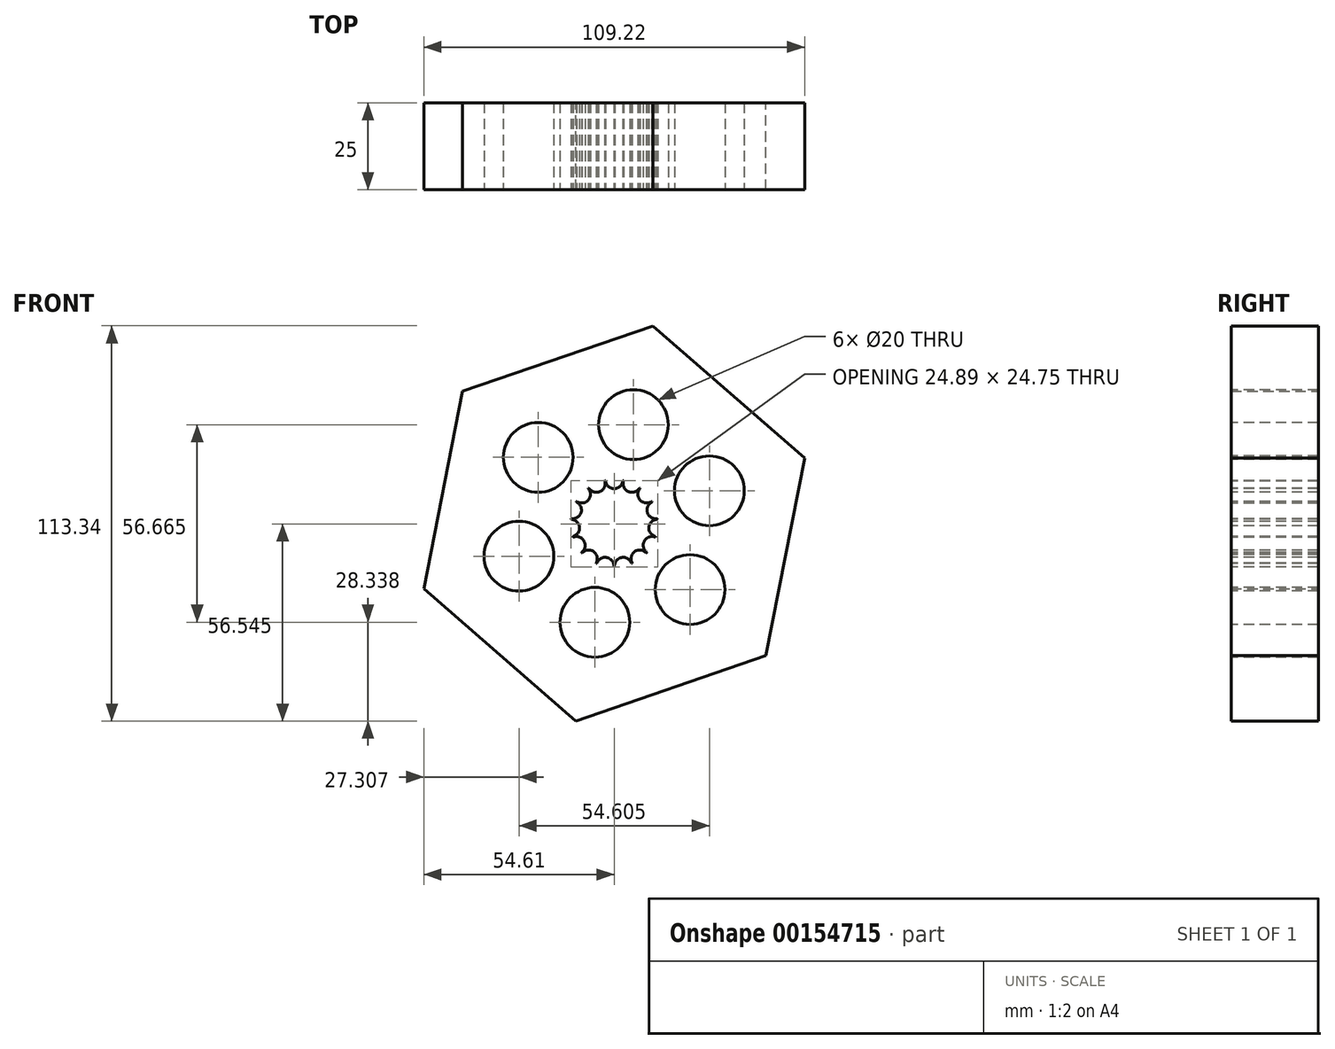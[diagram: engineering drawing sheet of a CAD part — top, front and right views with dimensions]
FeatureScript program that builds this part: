
annotation { "Feature Type Name" : "Feature", "Feature Type Description" : "" }
export const myFeature = defineFeature(function(context is Context, id is Id, definition is map)
    precondition{}
    {
        {
            var Q0;
            Q0=qCreatedBy(makeId("Front.planeOp"),FACE);
            var sketch = newSketch(context, id + "F0", { "sketchPlane" : qUnion([Q0])});
            skCircle(sketch, "E0.cCircle", {"center": v(0, 0) * mm, "radius": 50 * mm, "construction": true});
            skLineSegment(sketch, "E0.0", {"start": v(-11.06, -56.67) * mm, "end": v(-54.6, -18.75) * mm});
            skLineSegment(sketch, "E0.1", {"start": v(-54.6, -18.75) * mm, "end": v(-43.54, 37.91) * mm});
            skLineSegment(sketch, "E0.2", {"start": v(-43.54, 37.91) * mm, "end": v(11.06, 56.67) * mm});
            skLineSegment(sketch, "E0.3", {"start": v(11.06, 56.67) * mm, "end": v(54.6, 18.75) * mm});
            skLineSegment(sketch, "E0.4", {"start": v(54.6, 18.75) * mm, "end": v(43.54, -37.91) * mm});
            skLineSegment(sketch, "E0.5", {"start": v(43.54, -37.91) * mm, "end": v(-11.06, -56.67) * mm});
            skPoint(sketch, "E0.0.midPoint", {"position": v(-32.83, -37.7) * mm});
            skSolve(sketch);
        }
        {
            var Q0;
            Q0=makeQuery(id+"F0.imprint","IMPRINT",FACE,{"disambiguationData":[TD([[makeQuery(id+"F0.imprint","IMPRINT",EDGE,{"derivedFrom":sQuery(id+"F0.wireOp",EDGE,"E0.0")}),-1.0]])]});
            extrude(context, id + "F1", {"entities" : qUnion([Q0]), "endBound" : BoundingType.SYMMETRIC, "depth" : 25 * mm});
        }
        {
            var Q0;
            Q0=makeQuery(id+"F1.opExtrude","CAP_FACE",FACE,{"disambiguationData":[OSD([sQuery(id+"F0.wireOp",EDGE,"E0.0"),sQuery(id+"F0.wireOp",EDGE,"E0.1"),sQuery(id+"F0.wireOp",EDGE,"E0.2"),sQuery(id+"F0.wireOp",EDGE,"E0.3"),sQuery(id+"F0.wireOp",EDGE,"E0.4"),sQuery(id+"F0.wireOp",EDGE,"E0.5")])],"isStart":false});
            var sketch = newSketch(context, id + "F2", { "sketchPlane" : qUnion([Q0])});
            skLineSegment(sketch, "E1", {"start": v(-43.54, 37.91) * mm, "end": v(54.6, 18.75) * mm, "construction": true});
            skLineSegment(sketch, "E2", {"start": v(-11.06, -56.67) * mm, "end": v(11.06, 56.67) * mm, "construction": true});
            skLineSegment(sketch, "E3", {"start": v(-54.6, -18.75) * mm, "end": v(43.54, -37.91) * mm, "construction": true});
            skCircle(sketch, "E4", {"center": v(5.53, 28.33) * mm, "radius": 10 * mm});
            skCircle(sketch, "E5.1.0", {"center": v(-21.77, 18.96) * mm, "radius": 10 * mm});
            skCircle(sketch, "E5.2.0", {"center": v(-27.3, -9.38) * mm, "radius": 10 * mm});
            skCircle(sketch, "E5.3.0", {"center": v(-5.53, -28.33) * mm, "radius": 10 * mm});
            skCircle(sketch, "E5.4.0", {"center": v(21.77, -18.96) * mm, "radius": 10 * mm});
            skCircle(sketch, "E5.5.0", {"center": v(27.3, 9.38) * mm, "radius": 10 * mm});
            skPoint(sketch, "E5.center", {"position": v(0, 0) * mm});
            skSolve(sketch);
        }
        {
            var Q0;
            Q0=makeQuery(id+"F2.imprint","IMPRINT",FACE,{"disambiguationData":[TD([[makeQuery(id+"F2.imprint","IMPRINT",EDGE,{"derivedFrom":sQuery(id+"F2.wireOp",EDGE,"E4")}),1.0]])]});
            var Q1;
            Q1=makeQuery(id+"F2.imprint","IMPRINT",FACE,{"disambiguationData":[TD([[makeQuery(id+"F2.imprint","IMPRINT",EDGE,{"derivedFrom":sQuery(id+"F2.wireOp",EDGE,"E5.5.0")}),1.0]])]});
            var Q2;
            Q2=makeQuery(id+"F2.imprint","IMPRINT",FACE,{"disambiguationData":[TD([[makeQuery(id+"F2.imprint","IMPRINT",EDGE,{"derivedFrom":sQuery(id+"F2.wireOp",EDGE,"E5.4.0")}),1.0]])]});
            var Q3;
            Q3=makeQuery(id+"F2.imprint","IMPRINT",FACE,{"disambiguationData":[TD([[makeQuery(id+"F2.imprint","IMPRINT",EDGE,{"derivedFrom":sQuery(id+"F2.wireOp",EDGE,"E5.3.0")}),1.0]])]});
            var Q4;
            Q4=makeQuery(id+"F2.imprint","IMPRINT",FACE,{"disambiguationData":[TD([[makeQuery(id+"F2.imprint","IMPRINT",EDGE,{"derivedFrom":sQuery(id+"F2.wireOp",EDGE,"E5.2.0")}),1.0]])]});
            var Q5;
            Q5=makeQuery(id+"F2.imprint","IMPRINT",FACE,{"disambiguationData":[TD([[makeQuery(id+"F2.imprint","IMPRINT",EDGE,{"derivedFrom":sQuery(id+"F2.wireOp",EDGE,"E5.1.0")}),1.0]])]});
            extrude(context, id + "F3", {"entities" : qUnion([Q0, Q1, Q2, Q3, Q4, Q5]), "operationType" : NewBodyOperationType.REMOVE, "oppositeDirection" : true, "depth" : 25 * mm});
        }
        {
            var Q0;
            Q0=makeQuery(id+"F1.opExtrude","CAP_FACE",FACE,{"disambiguationData":[OSD([sQuery(id+"F0.wireOp",EDGE,"E0.0"),sQuery(id+"F0.wireOp",EDGE,"E0.1"),sQuery(id+"F0.wireOp",EDGE,"E0.2"),sQuery(id+"F0.wireOp",EDGE,"E0.3"),sQuery(id+"F0.wireOp",EDGE,"E0.4"),sQuery(id+"F0.wireOp",EDGE,"E0.5")])],"isStart":false});
            var sketch = newSketch(context, id + "F4", { "sketchPlane" : qUnion([Q0])});
            skArc(sketch, "E6", {"start": v(-2.49, 12.25) * mm, "mid": v(-2.6, 12.23) * mm, "end": v(-2.71, 12.2) * mm});
            skArc(sketch, "E7", {"start": v(-2.49, 12.25) * mm, "mid": v(0, 10) * mm, "end": v(2.49, 12.25) * mm});
            skArc(sketch, "E8.1.0", {"start": v(2.71, 12.2) * mm, "mid": v(4.07, 9.14) * mm, "end": v(7.25, 10.18) * mm});
            skArc(sketch, "E8.2.0", {"start": v(7.44, 10.05) * mm, "mid": v(7.43, 6.7) * mm, "end": v(10.77, 6.35) * mm});
            skArc(sketch, "E8.3.0", {"start": v(10.88, 6.15) * mm, "mid": v(9.51, 3.1) * mm, "end": v(12.42, 1.42) * mm});
            skArc(sketch, "E8.4.0", {"start": v(12.44, 1.2) * mm, "mid": v(9.95, -1.05) * mm, "end": v(11.92, -3.75) * mm});
            skArc(sketch, "E8.5.0", {"start": v(11.85, -3.97) * mm, "mid": v(8.66, -5) * mm, "end": v(9.37, -8.28) * mm});
            skArc(sketch, "E8.6.0", {"start": v(9.21, -8.45) * mm, "mid": v(5.88, -8.1) * mm, "end": v(5.19, -11.37) * mm});
            skArc(sketch, "E8.7.0", {"start": v(4.98, -11.47) * mm, "mid": v(2.08, -9.78) * mm, "end": v(0.11, -12.5) * mm});
            skArc(sketch, "E8.8.0", {"start": v(-0.11, -12.5) * mm, "mid": v(-2.08, -9.78) * mm, "end": v(-4.98, -11.47) * mm});
            skArc(sketch, "E8.9.0", {"start": v(-5.19, -11.37) * mm, "mid": v(-5.88, -8.1) * mm, "end": v(-9.21, -8.45) * mm});
            skArc(sketch, "E8.10.0", {"start": v(-9.37, -8.28) * mm, "mid": v(-8.66, -5) * mm, "end": v(-11.85, -3.97) * mm});
            skArc(sketch, "E8.11.0", {"start": v(-11.92, -3.75) * mm, "mid": v(-9.95, -1.05) * mm, "end": v(-12.44, 1.2) * mm});
            skArc(sketch, "E8.12.0", {"start": v(-12.42, 1.42) * mm, "mid": v(-9.51, 3.1) * mm, "end": v(-10.88, 6.15) * mm});
            skArc(sketch, "E8.13.0", {"start": v(-10.77, 6.35) * mm, "mid": v(-7.43, 6.7) * mm, "end": v(-7.44, 10.05) * mm});
            skArc(sketch, "E8.14.0", {"start": v(-7.25, 10.18) * mm, "mid": v(-4.07, 9.14) * mm, "end": v(-2.71, 12.2) * mm});
            skLineSegment(sketch, "E8.anchor1", {"start": v(0, 0) * mm, "end": v(-2.49, 12.25) * mm, "construction": true});
            skLineSegment(sketch, "E8.anchor2", {"start": v(0, 0) * mm, "end": v(-7.25, 10.18) * mm, "construction": true});
            skArc(sketch, "E9.trimOffspring", {"start": v(2.71, 12.2) * mm, "mid": v(2.6, 12.23) * mm, "end": v(2.49, 12.25) * mm});
            skArc(sketch, "E10.trimOffspring", {"start": v(7.44, 10.05) * mm, "mid": v(7.35, 10.11) * mm, "end": v(7.25, 10.18) * mm});
            skArc(sketch, "E11.trimOffspring", {"start": v(10.88, 6.15) * mm, "mid": v(10.83, 6.25) * mm, "end": v(10.77, 6.35) * mm});
            skArc(sketch, "E12.trimOffspring", {"start": v(12.44, 1.2) * mm, "mid": v(12.43, 1.3) * mm, "end": v(12.42, 1.42) * mm});
            skArc(sketch, "E13.trimOffspring", {"start": v(11.85, -3.97) * mm, "mid": v(11.89, -3.86) * mm, "end": v(11.92, -3.75) * mm});
            skArc(sketch, "E14.trimOffspring", {"start": v(9.21, -8.45) * mm, "mid": v(9.29, -8.36) * mm, "end": v(9.37, -8.28) * mm});
            skArc(sketch, "E15.trimOffspring", {"start": v(4.98, -11.47) * mm, "mid": v(5.08, -11.42) * mm, "end": v(5.19, -11.37) * mm});
            skArc(sketch, "E16.trimOffspring", {"start": v(-0.11, -12.5) * mm, "mid": v(0, -12.5) * mm, "end": v(0.11, -12.5) * mm});
            skArc(sketch, "E17.trimOffspring", {"start": v(-5.19, -11.37) * mm, "mid": v(-5.08, -11.42) * mm, "end": v(-4.98, -11.47) * mm});
            skArc(sketch, "E18.trimOffspring", {"start": v(-9.37, -8.28) * mm, "mid": v(-9.29, -8.36) * mm, "end": v(-9.21, -8.45) * mm});
            skArc(sketch, "E19.trimOffspring", {"start": v(-11.92, -3.75) * mm, "mid": v(-11.89, -3.86) * mm, "end": v(-11.85, -3.97) * mm});
            skArc(sketch, "E20.trimOffspring", {"start": v(-12.42, 1.42) * mm, "mid": v(-12.43, 1.3) * mm, "end": v(-12.44, 1.2) * mm});
            skArc(sketch, "E21.trimOffspring", {"start": v(-10.77, 6.35) * mm, "mid": v(-10.83, 6.25) * mm, "end": v(-10.88, 6.15) * mm});
            skArc(sketch, "E22.trimOffspring", {"start": v(-7.25, 10.18) * mm, "mid": v(-7.35, 10.11) * mm, "end": v(-7.44, 10.05) * mm});
            skSolve(sketch);
        }
        {
            var Q0;
            Q0=makeQuery(id+"F4.imprint","IMPRINT",FACE,{"disambiguationData":[TD([[makeQuery(id+"F4.imprint","IMPRINT",EDGE,{"derivedFrom":sQuery(id+"F4.wireOp",EDGE,"E6")}),1.0]])]});
            extrude(context, id + "F5", {"entities" : qUnion([Q0]), "operationType" : NewBodyOperationType.REMOVE, "oppositeDirection" : true, "depth" : 25 * mm});
        }
    });
